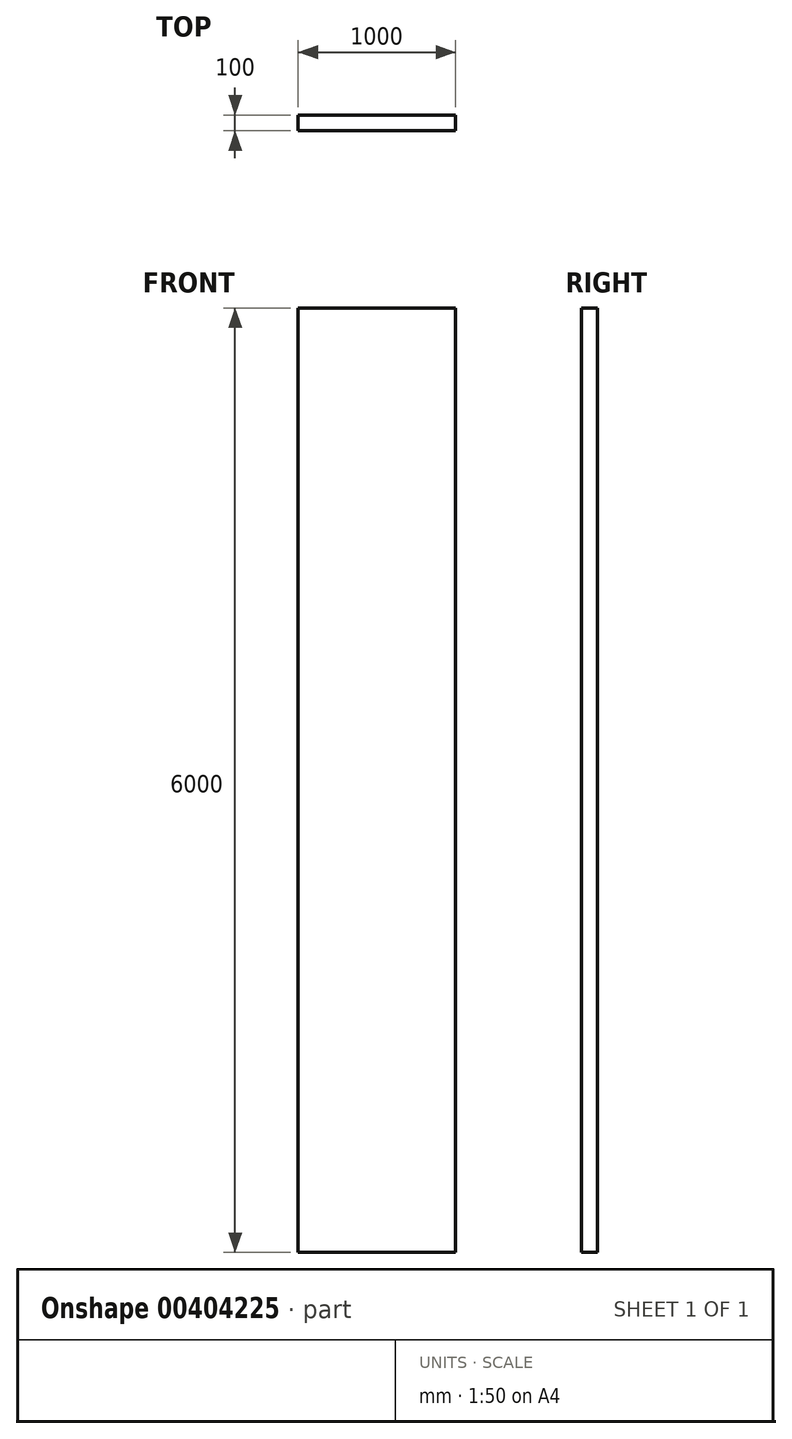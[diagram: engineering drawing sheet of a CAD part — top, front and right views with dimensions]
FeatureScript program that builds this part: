
annotation { "Feature Type Name" : "Feature", "Feature Type Description" : "" }
export const myFeature = defineFeature(function(context is Context, id is Id, definition is map)
    precondition{}
    {
        {
            var Q0;
            Q0=qCreatedBy(makeId("Front.planeOp"),FACE);
            var sketch = newSketch(context, id + "F0", { "sketchPlane" : qUnion([Q0])});
            skLineSegment(sketch, "E0.bottom", {"start": v(0, 0) * mm, "end": v(1000, 0) * mm});
            skLineSegment(sketch, "E0.top", {"start": v(0, 6000) * mm, "end": v(1000, 6000) * mm});
            skLineSegment(sketch, "E0.left", {"start": v(0, 0) * mm, "end": v(0, 6000) * mm});
            skLineSegment(sketch, "E0.right", {"start": v(1000, 0) * mm, "end": v(1000, 6000) * mm});
            skSolve(sketch);
        }
        {
            var Q0;
            Q0=makeQuery(id+"F0.imprint","IMPRINT",FACE,{"disambiguationData":[TD([[makeQuery(id+"F0.imprint","IMPRINT",EDGE,{"derivedFrom":sQuery(id+"F0.wireOp",EDGE,"E0.bottom")}),1.0]])]});
            extrude(context, id + "F1", {"entities" : qUnion([Q0]), "depth" : 100 * mm});
        }
    });
